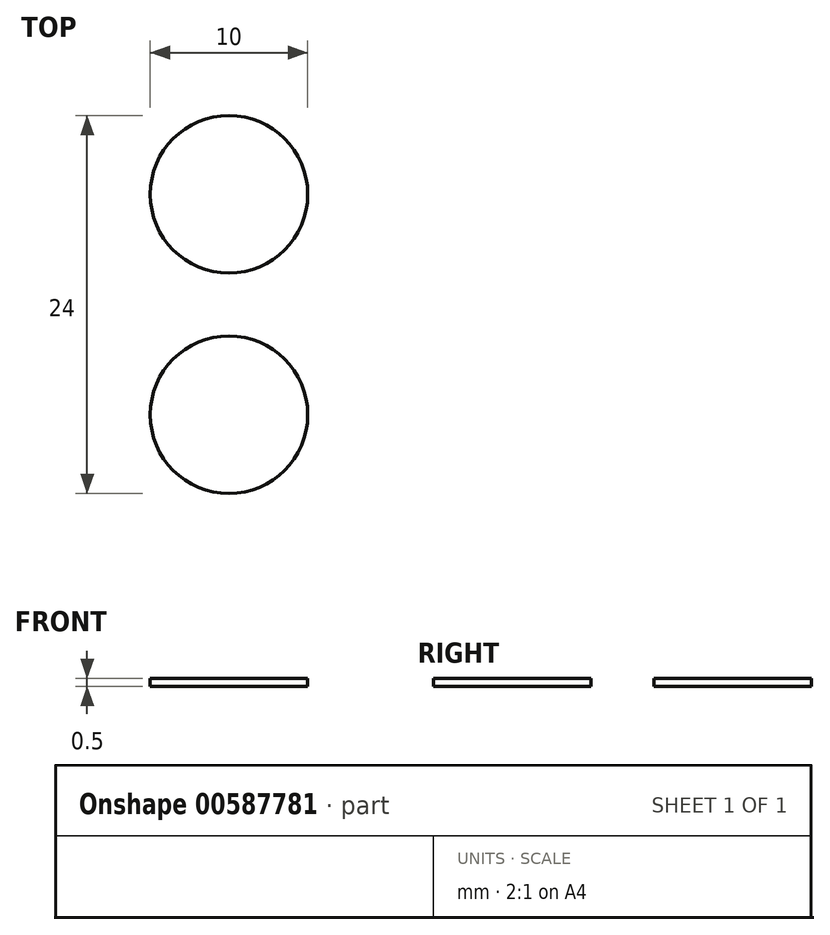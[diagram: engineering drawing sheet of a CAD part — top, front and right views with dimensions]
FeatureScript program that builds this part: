
annotation { "Feature Type Name" : "Feature", "Feature Type Description" : "" }
export const myFeature = defineFeature(function(context is Context, id is Id, definition is map)
    precondition{}
    {
        {
            var Q0;
            Q0=qCreatedBy(makeId("Top.planeOp"),FACE);
            var sketch = newSketch(context, id + "F0", { "sketchPlane" : qUnion([Q0])});
            skCircle(sketch, "E0", {"center": v(0, 7) * mm, "radius": 5 * mm});
            skCircle(sketch, "E1", {"center": v(0, -7) * mm, "radius": 5 * mm});
            skSolve(sketch);
        }
        {
            var Q0;
            Q0=makeQuery(id+"F0.imprint","IMPRINT",FACE,{"disambiguationData":[TD([[makeQuery(id+"F0.imprint","IMPRINT",EDGE,{"derivedFrom":sQuery(id+"F0.wireOp",EDGE,"E0")}),1.0]])]});
            var Q1;
            Q1=makeQuery(id+"F0.imprint","IMPRINT",FACE,{"disambiguationData":[TD([[makeQuery(id+"F0.imprint","IMPRINT",EDGE,{"derivedFrom":sQuery(id+"F0.wireOp",EDGE,"E1")}),1.0]])]});
            extrude(context, id + "F1", {"entities" : qUnion([Q0, Q1]), "depth" : .5 * mm, "offsetDistance" : 25 * mm});
        }
    });
